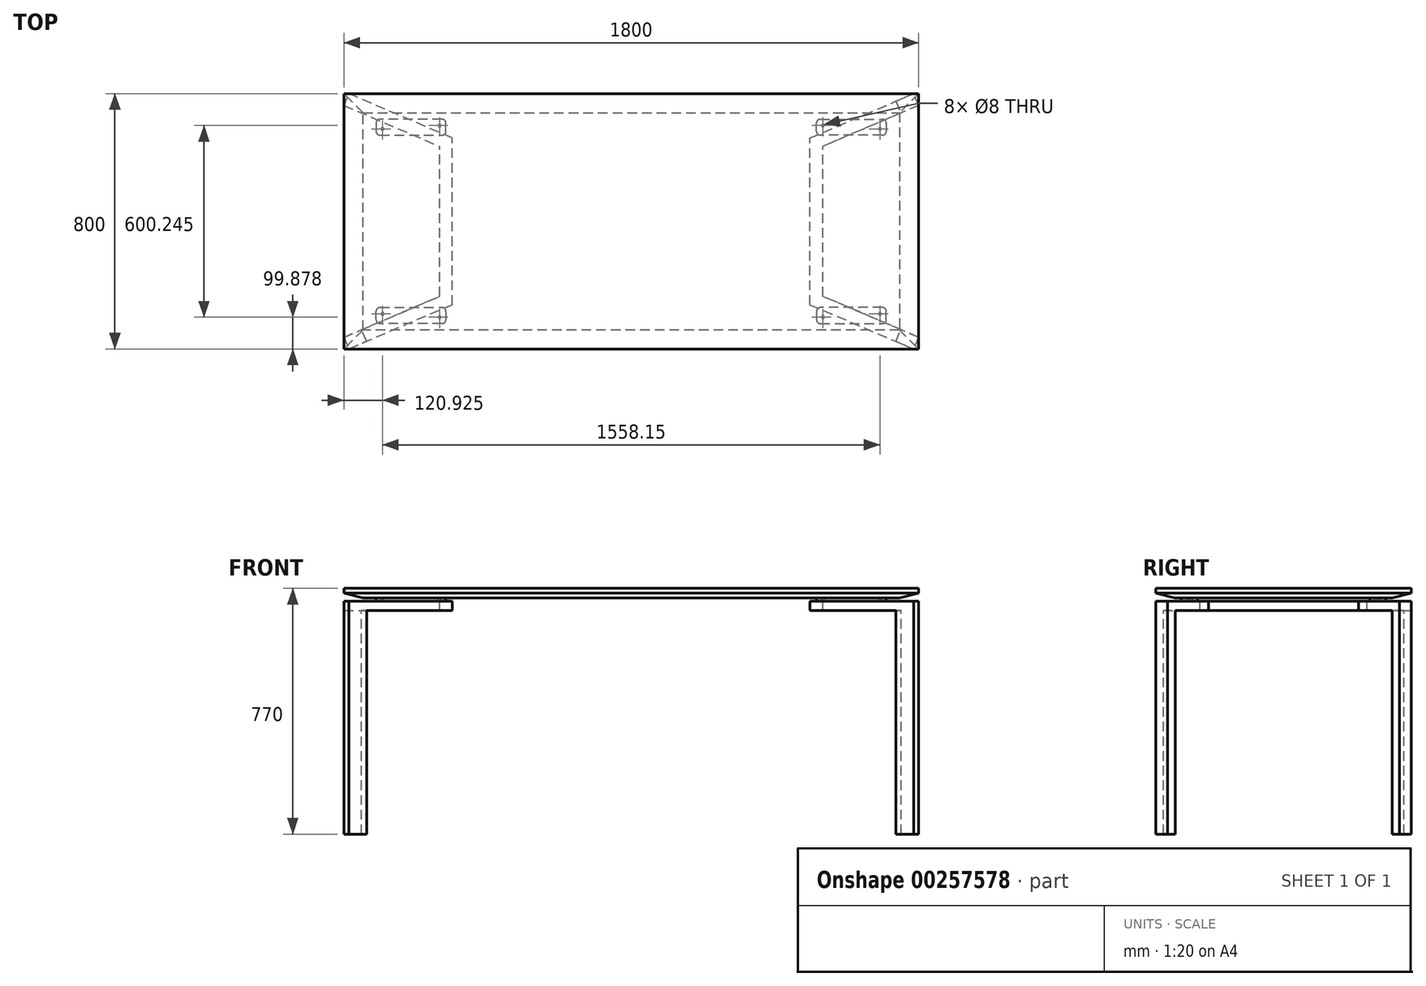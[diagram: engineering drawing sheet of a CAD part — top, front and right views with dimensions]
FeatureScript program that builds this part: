
annotation { "Feature Type Name" : "Feature", "Feature Type Description" : "" }
export const myFeature = defineFeature(function(context is Context, id is Id, definition is map)
    precondition{}
    {
        {
            var Q0;
            Q0=qCreatedBy(makeId("Top.planeOp"),FACE);
            var sketch = newSketch(context, id + "F0", { "sketchPlane" : qUnion([Q0])});
            skLineSegment(sketch, "E0.bottom", {"start": v(900, 400) * mm, "end": v(-900, 400) * mm});
            skLineSegment(sketch, "E0.top", {"start": v(900, -400) * mm, "end": v(-900, -400) * mm});
            skLineSegment(sketch, "E0.left", {"start": v(900, 400) * mm, "end": v(900, -400) * mm});
            skLineSegment(sketch, "E0.right", {"start": v(-900, 400) * mm, "end": v(-900, -400) * mm});
            skPoint(sketch, "E0.middle", {"position": v(0, 0) * mm});
            skSolve(sketch);
        }
        {
            var Q0;
            Q0=makeQuery(id+"F0.imprint","IMPRINT",FACE,{"disambiguationData":[TD([[makeQuery(id+"F0.imprint","IMPRINT",EDGE,{"derivedFrom":sQuery(id+"F0.wireOp",EDGE,"E0.bottom")}),1.0]])]});
            extrude(context, id + "F1", {"entities" : qUnion([Q0]), "depth" : 30 * mm});
        }
        {
            var Q0;
            Q0=makeQuery(id+"F1.opExtrude","CAP_EDGE",EDGE,{"disambiguationData":[OSD([sQuery(id+"F0.wireOp",EDGE,"E0.top")])],"isStart":true});
            var Q1;
            Q1=makeQuery(id+"F1.opExtrude","CAP_EDGE",EDGE,{"disambiguationData":[OSD([sQuery(id+"F0.wireOp",EDGE,"E0.right")])],"isStart":true});
            var Q2;
            Q2=makeQuery(id+"F1.opExtrude","CAP_EDGE",EDGE,{"disambiguationData":[OSD([sQuery(id+"F0.wireOp",EDGE,"E0.bottom")])],"isStart":true});
            var Q3;
            Q3=makeQuery(id+"F1.opExtrude","CAP_EDGE",EDGE,{"disambiguationData":[OSD([sQuery(id+"F0.wireOp",EDGE,"E0.left")])],"isStart":true});
            chamfer(context, id + "F2", {"entities" : qUnion([Q0, Q1, Q2, Q3]), "chamferType" : ChamferType.TWO_OFFSETS, "width1" : 15 * mm, "oppositeDirection" : true, "width2" : 60 * mm, "tangentPropagation" : true});
        }
        {
            var Q0;
            Q0=makeQuery(id+"F1.opExtrude","CAP_FACE",FACE,{"disambiguationData":[OSD([sQuery(id+"F0.wireOp",EDGE,"E0.bottom"),sQuery(id+"F0.wireOp",EDGE,"E0.top"),sQuery(id+"F0.wireOp",EDGE,"E0.left"),sQuery(id+"F0.wireOp",EDGE,"E0.right")])],"isStart":true});
            var sketch = newSketch(context, id + "F3", { "sketchPlane" : qUnion([Q0])});
            skLineSegment(sketch, "E1", {"start": v(592.35, 320) * mm, "end": v(786.95, 320) * mm});
            skLineSegment(sketch, "E2", {"start": v(798.95, 308) * mm, "end": v(798.95, 282) * mm});
            skLineSegment(sketch, "E3", {"start": v(786.95, 270) * mm, "end": v(592.35, 270) * mm});
            skLineSegment(sketch, "E4", {"start": v(580.35, 282) * mm, "end": v(580.35, 308) * mm});
            skLineSegment(sketch, "E5", {"start": v(0, 0) * mm, "end": v(192.76, 0) * mm, "construction": true});
            skLineSegment(sketch, "E6", {"start": v(0, 0) * mm, "end": v(0, -150.94) * mm, "construction": true});
            skLineSegment(sketch, "E7", {"start": v(-900, -363.22) * mm, "end": v(884.27, 400) * mm, "construction": true});
            skLineSegment(sketch, "E8", {"start": v(884.27, 400) * mm, "end": v(900, 363.22) * mm, "construction": true});
            skLineSegment(sketch, "E9", {"start": v(900, 363.22) * mm, "end": v(-884.27, -400) * mm, "construction": true});
            skLineSegment(sketch, "E10", {"start": v(-884.27, -400) * mm, "end": v(-900, -363.22) * mm, "construction": true});
            skPoint(sketch, "E11", {"position": v(580.35, 295) * mm});
            skPoint(sketch, "E12.visualSharp", {"position": v(580.35, 320) * mm});
            skArc(sketch, "E12.filletArc", {"start": v(592.35, 320) * mm, "mid": v(583.87, 316.49) * mm, "end": v(580.35, 308) * mm});
            skPoint(sketch, "E13.visualSharp", {"position": v(798.95, 270) * mm});
            skArc(sketch, "E13.filletArc", {"start": v(786.95, 270) * mm, "mid": v(795.44, 273.51) * mm, "end": v(798.95, 282) * mm});
            skPoint(sketch, "E14.visualSharp", {"position": v(798.95, 320) * mm});
            skArc(sketch, "E14.filletArc", {"start": v(798.95, 308) * mm, "mid": v(795.44, 316.49) * mm, "end": v(786.95, 320) * mm});
            skPoint(sketch, "E15.visualSharp", {"position": v(580.35, 270) * mm});
            skArc(sketch, "E15.filletArc", {"start": v(580.35, 282) * mm, "mid": v(583.87, 273.51) * mm, "end": v(592.35, 270) * mm});
            skCircle(sketch, "E16", {"center": v(600.23, 300.12) * mm, "radius": 19.88 * mm, "construction": true});
            skCircle(sketch, "E17", {"center": v(779.07, 289.88) * mm, "radius": 4 * mm});
            skLineSegment(sketch, "E18", {"start": v(580.35, 295) * mm, "end": v(798.95, 295) * mm, "construction": true});
            skCircle(sketch, "E19", {"center": v(600.23, 300.12) * mm, "radius": 4 * mm});
            skCircle(sketch, "E20", {"center": v(779.07, 289.88) * mm, "radius": 19.88 * mm, "construction": true});
            skSolve(sketch);
        }
        {
            var Q0;
            Q0=makeQuery(id+"F3.imprint","IMPRINT",FACE,{"disambiguationData":[TD([[makeQuery(id+"F3.imprint","IMPRINT",EDGE,{"derivedFrom":sQuery(id+"F3.wireOp",EDGE,"E1")}),-1.0]])]});
            var Q1;
            Q1=makeQuery(id+"F3.imprint","IMPRINT",FACE,{"disambiguationData":[TD([[makeQuery(id+"F3.imprint","IMPRINT",EDGE,{"derivedFrom":sQuery(id+"F3.wireOp",EDGE,"E1")}),-1.0]])]});
            var Q2;
            Q2=makeQuery(id+"F3.imprint","IMPRINT",FACE,{"disambiguationData":[TD([[makeQuery(id+"F3.imprint","IMPRINT",EDGE,{"derivedFrom":sQuery(id+"F3.wireOp",EDGE,"78456a59-0ad1-455a-a3a0-d7ed1f343e990.MirrorCS")}),1.0]])]});
            var Q3;
            Q3=makeQuery(id+"F3.imprint","IMPRINT",FACE,{"disambiguationData":[TD([[makeQuery(id+"F3.imprint","IMPRINT",EDGE,{"derivedFrom":sQuery(id+"F3.wireOp",EDGE,"c59880bb-1672-4030-b216-462686b6d9c90.MirrorCS")}),-1.0]])]});
            var Q4;
            Q4=makeQuery(id+"F3.imprint","IMPRINT",FACE,{"disambiguationData":[TD([[makeQuery(id+"F3.imprint","IMPRINT",EDGE,{"derivedFrom":sQuery(id+"F3.wireOp",EDGE,"88f59eff-e23c-4ac2-bf79-4ee49b3899eb0.MirrorCS")}),1.0]])]});
            extrude(context, id + "F4", {"entities" : qUnion([Q0, Q1, Q2, Q3, Q4]), "flatOperationType" : FlatOperationType.REMOVE, "offsetDistance" : 25 * mm, "depth" : 10 * mm, "domain" : OperationDomain.MODEL});
        }
        {
            var Q0;
            Q0=makeQuery(id+"F4.opExtrude","SWEPT_BODY",BODY,{"disambiguationData":[OSD([sQuery(id+"F3.wireOp",EDGE,"E1"),sQuery(id+"F3.wireOp",EDGE,"E2"),sQuery(id+"F3.wireOp",EDGE,"E3"),sQuery(id+"F3.wireOp",EDGE,"E4"),sQuery(id+"F3.wireOp",EDGE,"E12.filletArc"),sQuery(id+"F3.wireOp",EDGE,"E13.filletArc"),sQuery(id+"F3.wireOp",EDGE,"E14.filletArc"),sQuery(id+"F3.wireOp",EDGE,"E15.filletArc"),sQuery(id+"F3.wireOp",EDGE,"E17"),sQuery(id+"F3.wireOp",EDGE,"E19")])]});
            var Q1;
            Q1=qCreatedBy(makeId("Right.planeOp"),FACE);
            mirror(context, id + "F5", {"entities" : qUnion([Q0]), "mirrorPlane" : qUnion([Q1])});
        }
        {
            var Q0;
            Q0=makeQuery(id+"F5.opPattern","COPY",BODY,{"derivedFrom":makeQuery(id+"F4.opExtrude","SWEPT_BODY",BODY,{"disambiguationData":[OSD([sQuery(id+"F3.wireOp",EDGE,"E1"),sQuery(id+"F3.wireOp",EDGE,"E2"),sQuery(id+"F3.wireOp",EDGE,"E3"),sQuery(id+"F3.wireOp",EDGE,"E4"),sQuery(id+"F3.wireOp",EDGE,"E12.filletArc"),sQuery(id+"F3.wireOp",EDGE,"E13.filletArc"),sQuery(id+"F3.wireOp",EDGE,"E14.filletArc"),sQuery(id+"F3.wireOp",EDGE,"E15.filletArc"),sQuery(id+"F3.wireOp",EDGE,"E17"),sQuery(id+"F3.wireOp",EDGE,"E19")])]}),"instanceName":"1"});
            var Q1;
            Q1=makeQuery(id+"F4.opExtrude","SWEPT_BODY",BODY,{"disambiguationData":[OSD([sQuery(id+"F3.wireOp",EDGE,"E1"),sQuery(id+"F3.wireOp",EDGE,"E2"),sQuery(id+"F3.wireOp",EDGE,"E3"),sQuery(id+"F3.wireOp",EDGE,"E4"),sQuery(id+"F3.wireOp",EDGE,"E12.filletArc"),sQuery(id+"F3.wireOp",EDGE,"E13.filletArc"),sQuery(id+"F3.wireOp",EDGE,"E14.filletArc"),sQuery(id+"F3.wireOp",EDGE,"E15.filletArc"),sQuery(id+"F3.wireOp",EDGE,"E17"),sQuery(id+"F3.wireOp",EDGE,"E19")])]});
            var Q2;
            Q2=qCreatedBy(makeId("Front.planeOp"),FACE);
            mirror(context, id + "F6", {"entities" : qUnion([Q0, Q1]), "mirrorPlane" : qUnion([Q2])});
        }
        {
            var Q0;
            Q0=makeQuery(id+"F5.opPattern","COPY",FACE,{"derivedFrom":makeQuery(id+"F4.opExtrude","CAP_FACE",FACE,{"disambiguationData":[OSD([sQuery(id+"F3.wireOp",EDGE,"E1"),sQuery(id+"F3.wireOp",EDGE,"E2"),sQuery(id+"F3.wireOp",EDGE,"E3"),sQuery(id+"F3.wireOp",EDGE,"E4"),sQuery(id+"F3.wireOp",EDGE,"E12.filletArc"),sQuery(id+"F3.wireOp",EDGE,"E13.filletArc"),sQuery(id+"F3.wireOp",EDGE,"E14.filletArc"),sQuery(id+"F3.wireOp",EDGE,"E15.filletArc"),sQuery(id+"F3.wireOp",EDGE,"E17"),sQuery(id+"F3.wireOp",EDGE,"E19")])],"isStart":false}),"instanceName":"1"});
            var sketch = newSketch(context, id + "F7", { "sketchPlane" : qUnion([Q0])});
            skLineSegment(sketch, "E21", {"start": v(-900, 363.22) * mm, "end": v(-600, 234.9) * mm});
            skLineSegment(sketch, "E22", {"start": v(900, -363.22) * mm, "end": v(884.27, -400) * mm});
            skLineSegment(sketch, "E23", {"start": v(900, -363.22) * mm, "end": v(600, -234.9) * mm});
            skLineSegment(sketch, "E24", {"start": v(-900, 363.22) * mm, "end": v(-884.27, 400) * mm});
            skLineSegment(sketch, "E25", {"start": v(0, 0) * mm, "end": v(0, -250.76) * mm, "construction": true});
            skLineSegment(sketch, "E26.MirrorCS", {"start": v(-900, -363.22) * mm, "end": v(-600, -234.9) * mm});
            skLineSegment(sketch, "E27.MirrorCS", {"start": v(900, 363.22) * mm, "end": v(600, 234.9) * mm});
            skLineSegment(sketch, "E28.MirrorCS", {"start": v(-900, -363.22) * mm, "end": v(-884.27, -400) * mm});
            skLineSegment(sketch, "E29.MirrorCS", {"start": v(900, 363.22) * mm, "end": v(884.27, 400) * mm});
            skLineSegment(sketch, "E30", {"start": v(560, 261.3) * mm, "end": v(560, -261.3) * mm});
            skLineSegment(sketch, "E31", {"start": v(600, 234.9) * mm, "end": v(600, -234.9) * mm});
            skLineSegment(sketch, "E32.MirrorCS", {"start": v(-560, 261.3) * mm, "end": v(-560, -261.3) * mm});
            skLineSegment(sketch, "E33.MirrorCS", {"start": v(-600, 234.9) * mm, "end": v(-600, -234.9) * mm});
            skLineSegment(sketch, "E34.trimOffspring", {"start": v(-560, 261.3) * mm, "end": v(-884.27, 400) * mm});
            skLineSegment(sketch, "E35.trimOffspring", {"start": v(-560, -261.3) * mm, "end": v(-884.27, -400) * mm});
            skLineSegment(sketch, "E36.trimOffspring", {"start": v(560, -261.3) * mm, "end": v(884.27, -400) * mm});
            skLineSegment(sketch, "E37.trimOffspring", {"start": v(560, 261.3) * mm, "end": v(884.27, 400) * mm});
            skSolve(sketch);
        }
        {
            var Q0;
            {var subQ5=sQuery(id+"F7.wireOp",EDGE,"E28.MirrorCS");Q0=makeQuery(id+"F7.imprint","IMPRINT",FACE,{"disambiguationData":[TD([[makeQuery(id+"F7.imprint","IMPRINT",EDGE,{"derivedFrom":subQ5}),1.0]])]});}
            var Q1;
            {var subQ0=sQuery(id+"F7.wireOp",EDGE,"E26.MirrorCS");var subQ1=sQuery(id+"F7.wireOp",EDGE,"E21");var subQ2=makeQuery(id+"F7.imprint","INTERSECT",VERTEX,{"derivedFrom":[subQ1,subQ0]});Q1=makeQuery(id+"F7.imprint","IMPRINT",FACE,{"disambiguationData":[TD([[makeQuery(id+"F7.imprint","IMPRINT",EDGE,{"disambiguationData":[TD([[subQ2,1.0]])],"derivedFrom":subQ1}),1.0]])]});}
            var Q2;
            {var subQ0=sQuery(id+"F7.wireOp",EDGE,"E22");Q2=makeQuery(id+"F7.imprint","IMPRINT",FACE,{"disambiguationData":[TD([[makeQuery(id+"F7.imprint","IMPRINT",EDGE,{"derivedFrom":subQ0}),-1.0]])]});}
            var Q3;
            {var subQ5=sQuery(id+"F7.wireOp",EDGE,"E29.MirrorCS");Q3=makeQuery(id+"F7.imprint","IMPRINT",FACE,{"disambiguationData":[TD([[makeQuery(id+"F7.imprint","IMPRINT",EDGE,{"derivedFrom":subQ5}),1.0]])]});}
            var Q4;
            {var subQ0=sQuery(id+"F7.wireOp",EDGE,"E26.MirrorCS");var subQ1=sQuery(id+"F7.wireOp",EDGE,"E21");var subQ2=makeQuery(id+"F7.imprint","INTERSECT",VERTEX,{"derivedFrom":[subQ1,subQ0]});Q4=makeQuery(id+"F7.imprint","IMPRINT",FACE,{"disambiguationData":[TD([[makeQuery(id+"F7.imprint","IMPRINT",EDGE,{"disambiguationData":[TD([[subQ2,-1.0]])],"derivedFrom":subQ1}),1.0]])]});}
            var Q5;
            {var subQ0=sQuery(id+"F7.wireOp",EDGE,"E24");Q5=makeQuery(id+"F7.imprint","IMPRINT",FACE,{"disambiguationData":[TD([[makeQuery(id+"F7.imprint","IMPRINT",EDGE,{"derivedFrom":subQ0}),-1.0]])]});}
            var Q6;
            {var subQ0=sQuery(id+"F7.wireOp",EDGE,"E21");var subQ1=makeQuery(id+"F4.opExtrude","CAP_EDGE",EDGE,{"disambiguationData":[OSD([sQuery(id+"F3.wireOp",EDGE,"84202c8b-ab99-423c-9b24-0aa483fdb7260.MirrorCS")])],"isStart":false});var subQ2=makeQuery(id+"F7.imprint","INTERSECT",VERTEX,{"derivedFrom":[subQ1,subQ0]});Q6=makeQuery(id+"F7.imprint","IMPRINT",FACE,{"disambiguationData":[TD([[makeQuery(id+"F7.imprint","IMPRINT",EDGE,{"disambiguationData":[TD([[subQ2,-1.0]])],"derivedFrom":subQ0}),1.0]])]});}
            var Q7;
            {var subQ3=sQuery(id+"F7.wireOp",EDGE,"E21");var subQ9=makeQuery(id+"F5.opPattern","COPY",EDGE,{"derivedFrom":makeQuery(id+"F4.opExtrude","CAP_EDGE",EDGE,{"disambiguationData":[OSD([sQuery(id+"F3.wireOp",EDGE,"E14.filletArc")])],"isStart":false}),"instanceName":"1"});var subQ11=makeQuery(id+"F7.imprint","INTERSECT",VERTEX,{"derivedFrom":[subQ9,subQ3]});Q7=makeQuery(id+"F7.imprint","IMPRINT",FACE,{"disambiguationData":[TD([[makeQuery(id+"F7.imprint","IMPRINT",EDGE,{"disambiguationData":[TD([[subQ11,-1.0]])],"derivedFrom":subQ3}),1.0]])]});}
            extrude(context, id + "F8", {"entities" : qUnion([Q0, Q1, Q2, Q3, Q4, Q5, Q6, Q7]), "depth" : 30 * mm});
        }
        {
            var Q0;
            Q0=makeQuery(id+"F8.opExtrude","CAP_FACE",FACE,{"disambiguationData":[OSD([sQuery(id+"F7.wireOp",EDGE,"E21"),sQuery(id+"F7.wireOp",EDGE,"E22"),sQuery(id+"F7.wireOp",EDGE,"E23"),sQuery(id+"F7.wireOp",EDGE,"E24"),sQuery(id+"F7.wireOp",EDGE,"E26.MirrorCS"),sQuery(id+"F7.wireOp",EDGE,"E27.MirrorCS"),sQuery(id+"F7.wireOp",EDGE,"E28.MirrorCS"),sQuery(id+"F7.wireOp",EDGE,"E29.MirrorCS")])],"isStart":false});
            var sketch = newSketch(context, id + "F9", { "sketchPlane" : qUnion([Q0])});
            skLineSegment(sketch, "E38.bottom", {"start": v(884.27, 400) * mm, "end": v(829.1, 376.4) * mm});
            skLineSegment(sketch, "E38.top", {"start": v(900, 363.22) * mm, "end": v(844.83, 339.63) * mm});
            skLineSegment(sketch, "E38.left", {"start": v(884.27, 400) * mm, "end": v(900, 363.22) * mm});
            skLineSegment(sketch, "E38.right", {"start": v(829.1, 376.4) * mm, "end": v(844.83, 339.63) * mm});
            skPoint(sketch, "E38.middle", {"position": v(864.55, 369.81) * mm});
            skLineSegment(sketch, "E39", {"start": v(-900, -363.22) * mm, "end": v(682.56, 313.72) * mm});
            skLineSegment(sketch, "E40", {"start": v(0, 0) * mm, "end": v(477.3, 0) * mm, "construction": true});
            skLineSegment(sketch, "E41", {"start": v(0, 0) * mm, "end": v(0, -305.67) * mm, "construction": true});
            skLineSegment(sketch, "E42.MirrorCS", {"start": v(900, -363.22) * mm, "end": v(844.83, -339.63) * mm});
            skLineSegment(sketch, "E43.MirrorCS", {"start": v(884.27, -400) * mm, "end": v(829.1, -376.4) * mm});
            skLineSegment(sketch, "E44.MirrorCS", {"start": v(884.27, -400) * mm, "end": v(900, -363.22) * mm});
            skLineSegment(sketch, "E45.MirrorCS", {"start": v(829.1, -376.4) * mm, "end": v(844.83, -339.63) * mm});
            skLineSegment(sketch, "E46.MirrorCS", {"start": v(0, 0) * mm, "end": v(0, 305.67) * mm, "construction": true});
            skLineSegment(sketch, "E47.MirrorCS", {"start": v(-829.1, 376.4) * mm, "end": v(-844.83, 339.63) * mm});
            skLineSegment(sketch, "E48.MirrorCS", {"start": v(-884.27, 400) * mm, "end": v(-829.1, 376.4) * mm});
            skLineSegment(sketch, "E49.MirrorCS", {"start": v(-884.27, 400) * mm, "end": v(-900, 363.22) * mm});
            skLineSegment(sketch, "E50.MirrorCS", {"start": v(-900, 363.22) * mm, "end": v(-844.83, 339.63) * mm});
            skLineSegment(sketch, "E51.MirrorCS", {"start": v(-900, -363.22) * mm, "end": v(-844.83, -339.63) * mm});
            skLineSegment(sketch, "E52.MirrorCS", {"start": v(-829.1, -376.4) * mm, "end": v(-844.83, -339.63) * mm});
            skLineSegment(sketch, "E53.MirrorCS", {"start": v(-884.27, -400) * mm, "end": v(-829.1, -376.4) * mm});
            skLineSegment(sketch, "E54.MirrorCS", {"start": v(-884.27, -400) * mm, "end": v(-900, -363.22) * mm});
            skSolve(sketch);
        }
        {
            var Q0;
            Q0=makeQuery(id+"F9.imprint","IMPRINT",FACE,{"disambiguationData":[TD([[makeQuery(id+"F9.imprint","IMPRINT",EDGE,{"derivedFrom":sQuery(id+"F9.wireOp",EDGE,"E42.MirrorCS")}),1.0]])]});
            var Q1;
            Q1=makeQuery(id+"F9.imprint","IMPRINT",FACE,{"disambiguationData":[TD([[makeQuery(id+"F9.imprint","IMPRINT",EDGE,{"derivedFrom":sQuery(id+"F9.wireOp",EDGE,"E38.bottom")}),1.0]])]});
            var Q2;
            Q2=makeQuery(id+"F9.imprint","IMPRINT",FACE,{"disambiguationData":[TD([[makeQuery(id+"F9.imprint","IMPRINT",EDGE,{"derivedFrom":sQuery(id+"F9.wireOp",EDGE,"E47.MirrorCS")}),-1.0]])]});
            var Q3;
            Q3=makeQuery(id+"F9.imprint","IMPRINT",FACE,{"disambiguationData":[TD([[makeQuery(id+"F9.imprint","IMPRINT",EDGE,{"derivedFrom":sQuery(id+"F9.wireOp",EDGE,"E51.MirrorCS")}),-1.0]])]});
            var Q4;
            Q4=makeQuery(id+"F9.imprint","IMPRINT",FACE,{"disambiguationData":[TD([[makeQuery(id+"F9.imprint","IMPRINT",EDGE,{"derivedFrom":sQuery(id+"F9.wireOp",EDGE,"E38.bottom")}),-1.0]])]});
            extrude(context, id + "F10", {"entities" : qUnion([Q0, Q1, Q2, Q3, Q4]), "operationType" : NewBodyOperationType.ADD, "depth" : 700 * mm});
        }
    });
